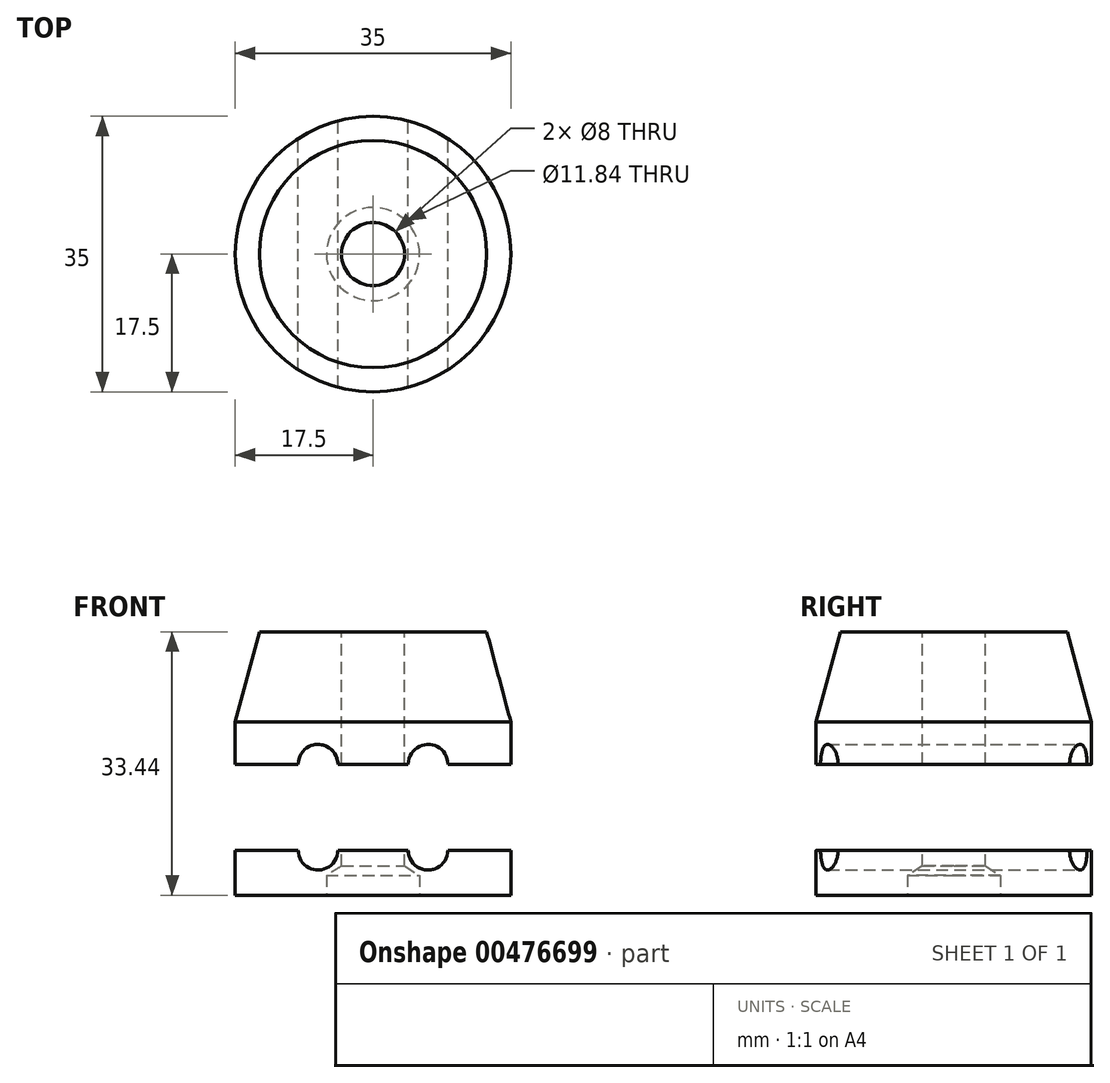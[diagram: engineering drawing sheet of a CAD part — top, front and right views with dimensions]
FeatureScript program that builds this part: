
annotation { "Feature Type Name" : "Feature", "Feature Type Description" : "" }
export const myFeature = defineFeature(function(context is Context, id is Id, definition is map)
    precondition{}
    {
        {
            var Q0;
            Q0=qCreatedBy(makeId("Front.planeOp"),FACE);
            var sketch = newSketch(context, id + "F0", { "sketchPlane" : qUnion([Q0])});
            skLineSegment(sketch, "E0", {"start": v(0, 0) * mm, "end": v(0, 11.43) * mm});
            skLineSegment(sketch, "E1.bottom", {"start": v(0, 11.43) * mm, "end": v(14.44, 11.43) * mm});
            skLineSegment(sketch, "E1.top", {"start": v(0, 0) * mm, "end": v(17.5, 0) * mm});
            skLineSegment(sketch, "E1.left", {"start": v(0, 11.43) * mm, "end": v(0, 0) * mm});
            skLineSegment(sketch, "E2.top", {"start": v(0, -5.38) * mm, "end": v(17.5, -5.38) * mm});
            skLineSegment(sketch, "E2.left", {"start": v(0, 0) * mm, "end": v(0, -5.38) * mm});
            skLineSegment(sketch, "E2.right", {"start": v(17.5, 0) * mm, "end": v(17.5, -5.38) * mm});
            skLineSegment(sketch, "E3", {"start": v(17.5, 0) * mm, "end": v(14.44, 11.43) * mm});
            skLineSegment(sketch, "E4.bottom", {"start": v(0, -5.38) * mm, "end": v(17.5, -5.38) * mm, "construction": true});
            skLineSegment(sketch, "E5.bottom", {"start": v(0, -16.3) * mm, "end": v(17.5, -16.3) * mm});
            skLineSegment(sketch, "E5.top", {"start": v(0, -22) * mm, "end": v(17.5, -22) * mm});
            skLineSegment(sketch, "E5.left", {"start": v(0, -16.3) * mm, "end": v(0, -22) * mm});
            skLineSegment(sketch, "E5.right", {"start": v(17.5, -16.3) * mm, "end": v(17.5, -22) * mm});
            skLineSegment(sketch, "E6", {"start": v(6.99, -25.21) * mm, "end": v(6.99, -16.3) * mm});
            skLineSegment(sketch, "E7.MirrorCS", {"start": v(0, -5.38) * mm, "end": v(-17.5, -5.38) * mm});
            skLineSegment(sketch, "E8.MirrorCS", {"start": v(0, -22) * mm, "end": v(-17.5, -22) * mm});
            skLineSegment(sketch, "E9.MirrorCS", {"start": v(0, -16.3) * mm, "end": v(-17.5, -16.3) * mm});
            skLineSegment(sketch, "E10.MirrorCS", {"start": v(-6.98, -25.21) * mm, "end": v(-6.99, -16.3) * mm});
            skLineSegment(sketch, "E11.MirrorCS", {"start": v(-17.5, 0) * mm, "end": v(-14.44, 11.43) * mm});
            skLineSegment(sketch, "E12.MirrorCS", {"start": v(-17.5, 0) * mm, "end": v(-17.5, -5.38) * mm});
            skLineSegment(sketch, "E13.MirrorCS", {"start": v(-17.5, -16.3) * mm, "end": v(-17.5, -22) * mm});
            skLineSegment(sketch, "E14.MirrorCS", {"start": v(0, 0) * mm, "end": v(-17.5, 0) * mm});
            skLineSegment(sketch, "E15.MirrorCS", {"start": v(0, 11.43) * mm, "end": v(-14.44, 11.43) * mm});
            skLineSegment(sketch, "E16.trimOffspring", {"start": v(-6.99, -5.38) * mm, "end": v(-6.99, 10.66) * mm});
            skLineSegment(sketch, "E17.trimOffspring", {"start": v(6.98, -5.38) * mm, "end": v(6.98, 10.66) * mm});
            skSolve(sketch);
        }
        {
            var Q0;
            {var subQ0=sQuery(id+"F0.wireOp",EDGE,"E1.left");Q0=makeQuery(id+"F0.imprint","IMPRINT",FACE,{"disambiguationData":[TD([[makeQuery(id+"F0.imprint","IMPRINT",EDGE,{"derivedFrom":subQ0}),1.0]])]});}
            var Q1;
            {var subQ0=sQuery(id+"F0.wireOp",EDGE,"E3");Q1=makeQuery(id+"F0.imprint","IMPRINT",FACE,{"disambiguationData":[TD([[makeQuery(id+"F0.imprint","IMPRINT",EDGE,{"derivedFrom":subQ0}),1.0]])]});}
            var Q2;
            {var subQ0=sQuery(id+"F0.wireOp",EDGE,"E2.right");Q2=makeQuery(id+"F0.imprint","IMPRINT",FACE,{"disambiguationData":[TD([[makeQuery(id+"F0.imprint","IMPRINT",EDGE,{"derivedFrom":subQ0}),-1.0]])]});}
            var Q3;
            {var subQ0=sQuery(id+"F0.wireOp",EDGE,"E2.left");Q3=makeQuery(id+"F0.imprint","IMPRINT",FACE,{"disambiguationData":[TD([[makeQuery(id+"F0.imprint","IMPRINT",EDGE,{"derivedFrom":subQ0}),1.0]])]});}
            var Q4;
            {var subQ0=sQuery(id+"F0.wireOp",EDGE,"E5.left");Q4=makeQuery(id+"F0.imprint","IMPRINT",FACE,{"disambiguationData":[TD([[makeQuery(id+"F0.imprint","IMPRINT",EDGE,{"derivedFrom":subQ0}),1.0]])]});}
            var Q5;
            {var subQ0=sQuery(id+"F0.wireOp",EDGE,"E5.right");Q5=makeQuery(id+"F0.imprint","IMPRINT",FACE,{"disambiguationData":[TD([[makeQuery(id+"F0.imprint","IMPRINT",EDGE,{"derivedFrom":subQ0}),-1.0]])]});}
            var Q6;
            Q6=sQuery(id+"F0.wireOp",EDGE,"E1.left");
            revolve(context, id + "F1", {"entities" : qUnion([Q0, Q1, Q2, Q3, Q4, Q5]), "axis" : qUnion([Q6]), "revolveType" : RevolveType.FULL});
        }
        {
            var Q0;
            Q0=sQuery(id+"F0.wireOp",VERTEX,"E17.trimOffspring.start");
            var Q1;
            Q1=sQuery(id+"F0.wireOp",VERTEX,"E16.trimOffspring.start");
            var Q2;
            Q2=sQuery(id+"F0.wireOp",VERTEX,"E6.end");
            var Q3;
            Q3=sQuery(id+"F0.wireOp",VERTEX,"E10.MirrorCS.end");
            var Q4;
            Q4=makeQuery(id+"F1.opRevolve","SWEPT_BODY",BODY,{"disambiguationData":[OSD([sQuery(id+"F0.wireOp",EDGE,"E1.bottom"),sQuery(id+"F0.wireOp",EDGE,"E2.top"),sQuery(id+"F0.wireOp",EDGE,"E2.right"),sQuery(id+"F0.wireOp",EDGE,"E3"),sQuery(id+"F0.wireOp",EDGE,"E1.left"),sQuery(id+"F0.wireOp",EDGE,"E2.left")])]});
            var Q5;
            Q5=makeQuery(id+"F1.opRevolve","SWEPT_BODY",BODY,{"disambiguationData":[OSD([sQuery(id+"F0.wireOp",EDGE,"E5.bottom"),sQuery(id+"F0.wireOp",EDGE,"E5.top"),sQuery(id+"F0.wireOp",EDGE,"E5.right"),sQuery(id+"F0.wireOp",EDGE,"E5.left")])]});
            hole(context, id + "F2", {"style" : HoleStyle.SIMPLE, "endStyle" : HoleEndStyle.THROUGH, "oppositeDirection" : true, "holeDiameter" : 5.05 * mm, "isTappedThrough" : true, "tappedDepth" : 12.7 * mm, "tapClearance" : 3, "startFromSketch" : true, "locations" : qUnion([Q0, Q1, Q2, Q3]), "scope" : qUnion([Q4, Q5])});
        }
        {
            var Q0;
            Q0=sQuery(id+"F0.wireOp",VERTEX,"E16.trimOffspring.start");
            var Q1;
            Q1=sQuery(id+"F0.wireOp",VERTEX,"E17.trimOffspring.start");
            var Q2;
            Q2=sQuery(id+"F0.wireOp",VERTEX,"E6.end");
            var Q3;
            Q3=sQuery(id+"F0.wireOp",VERTEX,"E10.MirrorCS.end");
            var Q4;
            Q4=makeQuery(id+"F1.opRevolve","SWEPT_BODY",BODY,{"disambiguationData":[OSD([sQuery(id+"F0.wireOp",EDGE,"E1.bottom"),sQuery(id+"F0.wireOp",EDGE,"E2.top"),sQuery(id+"F0.wireOp",EDGE,"E2.right"),sQuery(id+"F0.wireOp",EDGE,"E3"),sQuery(id+"F0.wireOp",EDGE,"E1.left"),sQuery(id+"F0.wireOp",EDGE,"E2.left")])]});
            var Q5;
            Q5=makeQuery(id+"F1.opRevolve","SWEPT_BODY",BODY,{"disambiguationData":[OSD([sQuery(id+"F0.wireOp",EDGE,"E5.bottom"),sQuery(id+"F0.wireOp",EDGE,"E5.top"),sQuery(id+"F0.wireOp",EDGE,"E5.right"),sQuery(id+"F0.wireOp",EDGE,"E5.left")])]});
            hole(context, id + "F3", {"style" : HoleStyle.SIMPLE, "endStyle" : HoleEndStyle.THROUGH, "holeDiameter" : 5.05 * mm, "isTappedThrough" : true, "tappedDepth" : 12.7 * mm, "tapClearance" : 3, "startFromSketch" : true, "locations" : qUnion([Q0, Q1, Q2, Q3]), "scope" : qUnion([Q4, Q5])});
        }
        {
            var Q0;
            Q0=makeQuery(id+"F1.opRevolve","SWEPT_FACE",FACE,{"disambiguationData":[OSD([sQuery(id+"F0.wireOp",EDGE,"E1.bottom")])]});
            var sketch = newSketch(context, id + "F4", { "sketchPlane" : qUnion([Q0])});
            skCircle(sketch, "E18", {"center": v(0, 0) * mm, "radius": 4 * mm});
            skSolve(sketch);
        }
        {
            var Q0;
            Q0=sQuery(id+"F4.wireOp",VERTEX,"E18.center");
            var Q1;
            Q1=makeQuery(id+"F1.opRevolve","SWEPT_BODY",BODY,{"disambiguationData":[OSD([sQuery(id+"F0.wireOp",EDGE,"E1.bottom"),sQuery(id+"F0.wireOp",EDGE,"E2.top"),sQuery(id+"F0.wireOp",EDGE,"E2.right"),sQuery(id+"F0.wireOp",EDGE,"E3"),sQuery(id+"F0.wireOp",EDGE,"E1.left"),sQuery(id+"F0.wireOp",EDGE,"E2.left")])]});
            var Q2;
            Q2=makeQuery(id+"F1.opRevolve","SWEPT_BODY",BODY,{"disambiguationData":[OSD([sQuery(id+"F0.wireOp",EDGE,"E5.bottom"),sQuery(id+"F0.wireOp",EDGE,"E5.top"),sQuery(id+"F0.wireOp",EDGE,"E5.right"),sQuery(id+"F0.wireOp",EDGE,"E5.left")])]});
            hole(context, id + "F5", {"style" : HoleStyle.SIMPLE, "endStyle" : HoleEndStyle.THROUGH, "holeDiameter" : 8 * mm, "isTappedThrough" : true, "tappedDepth" : 12.7 * mm, "tapClearance" : 3, "startFromSketch" : true, "locations" : qUnion([Q0]), "scope" : qUnion([Q1, Q2])});
        }
        {
            var Q0;
            Q0=makeQuery(id+"F1.opRevolve","SWEPT_FACE",FACE,{"disambiguationData":[OSD([sQuery(id+"F0.wireOp",EDGE,"E5.top")])]});
            var sketch = newSketch(context, id + "F6", { "sketchPlane" : qUnion([Q0])});
            skCircle(sketch, "E19", {"center": v(0, 0) * mm, "radius": 5.92 * mm});
            skSolve(sketch);
        }
        {
            var Q0;
            Q0=sQuery(id+"F6.wireOp",VERTEX,"E19.center");
            var Q1;
            Q1=makeQuery(id+"F1.opRevolve","SWEPT_BODY",BODY,{"disambiguationData":[OSD([sQuery(id+"F0.wireOp",EDGE,"E5.bottom"),sQuery(id+"F0.wireOp",EDGE,"E5.top"),sQuery(id+"F0.wireOp",EDGE,"E5.right"),sQuery(id+"F0.wireOp",EDGE,"E5.left")])]});
            hole(context, id + "F7", {"style" : HoleStyle.SIMPLE, "endStyle" : HoleEndStyle.BLIND, "holeDiameter" : 11.84 * mm, "holeDepth" : 2.54 * mm, "isTappedThrough" : true, "tappedDepth" : 12.7 * mm, "tapClearance" : 3, "startFromSketch" : true, "locations" : qUnion([Q0]), "scope" : qUnion([Q1])});
        }
    });
